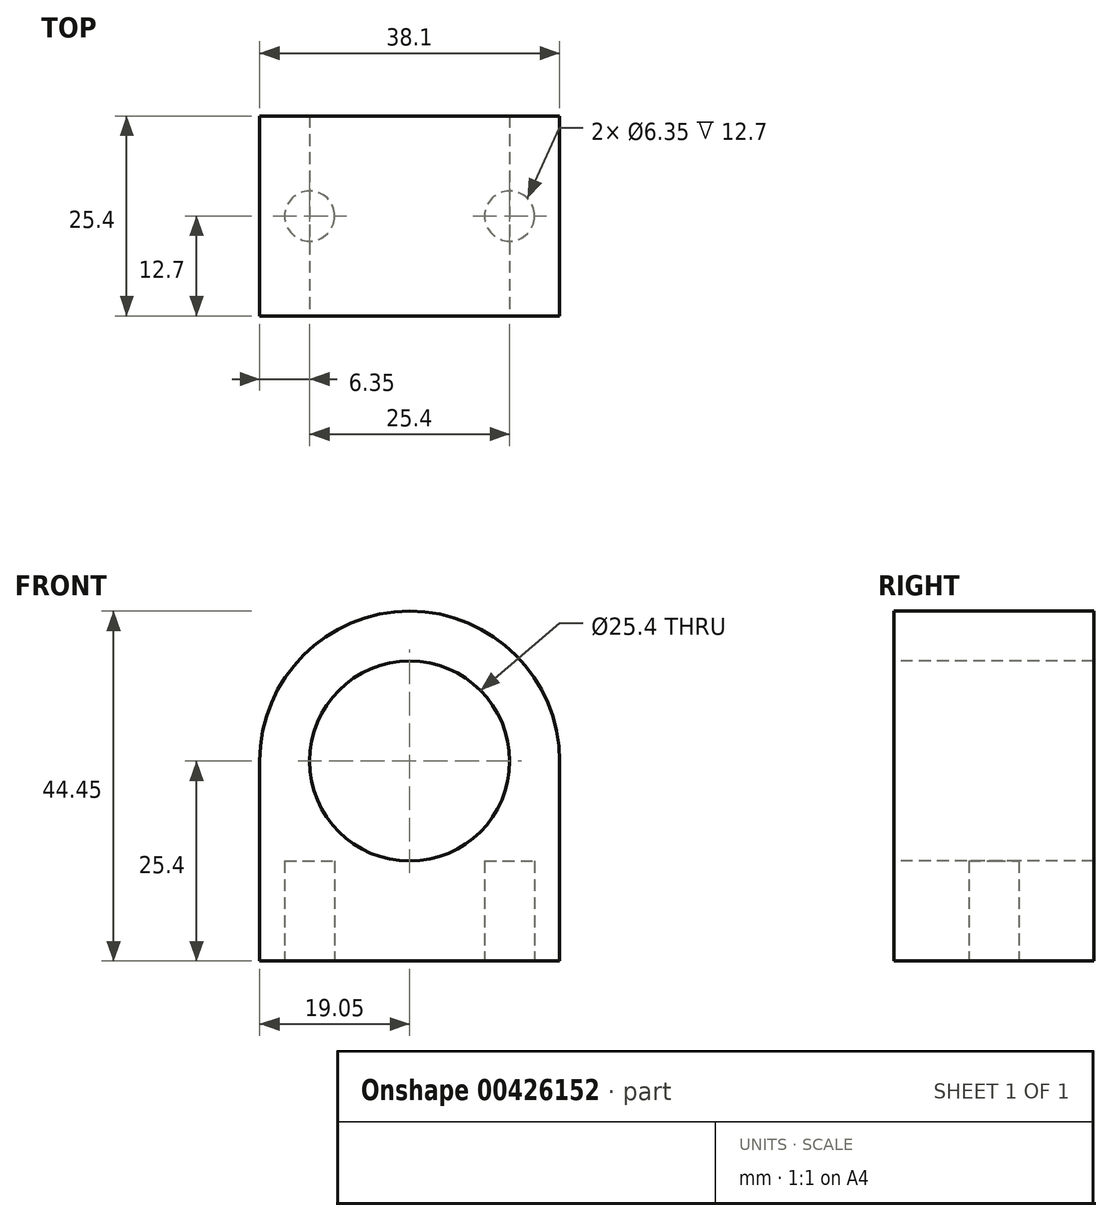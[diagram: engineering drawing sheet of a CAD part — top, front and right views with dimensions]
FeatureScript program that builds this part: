
annotation { "Feature Type Name" : "Feature", "Feature Type Description" : "" }
export const myFeature = defineFeature(function(context is Context, id is Id, definition is map)
    precondition{}
    {
        {
            var Q0;
            Q0=qCreatedBy(makeId("Front.planeOp"),FACE);
            var sketch = newSketch(context, id + "F0", { "sketchPlane" : qUnion([Q0])});
            skLineSegment(sketch, "E0.top", {"start": v(-19.05, -25.4) * mm, "end": v(19.05, -25.4) * mm});
            skLineSegment(sketch, "E0.left", {"start": v(-19.05, 0) * mm, "end": v(-19.05, -25.4) * mm});
            skLineSegment(sketch, "E0.right", {"start": v(19.05, 0) * mm, "end": v(19.05, -25.4) * mm});
            skArc(sketch, "E1", {"start": v(19.05, 0) * mm, "mid": v(0, 19.05) * mm, "end": v(-19.05, 0) * mm});
            skSolve(sketch);
        }
        {
            var Q0;
            Q0 = qSketchRegion(id + "F0", true);
            extrude(context, id + "F1", {"entities" : qUnion([Q0]), "endBound" : BoundingType.SYMMETRIC, "depth" : 25.4 * mm});
        }
        {
            var Q0;
            Q0=makeQuery(id+"F1.opExtrude","CAP_FACE",FACE,{"disambiguationData":[OSD([sQuery(id+"F0.wireOp",EDGE,"E0.top"),sQuery(id+"F0.wireOp",EDGE,"E0.left"),sQuery(id+"F0.wireOp",EDGE,"E0.right"),sQuery(id+"F0.wireOp",EDGE,"E1")])],"isStart":false});
            var sketch = newSketch(context, id + "F2", { "sketchPlane" : qUnion([Q0])});
            skCircle(sketch, "E2", {"center": v(0, 0) * mm, "radius": 12.7 * mm});
            skSolve(sketch);
        }
        {
            var Q0;
            Q0 = qSketchRegion(id + "F2", true);
            extrude(context, id + "F3", {"entities" : qUnion([Q0]), "operationType" : NewBodyOperationType.REMOVE, "endBound" : BoundingType.THROUGH_ALL, "oppositeDirection" : true, "depth" : 25.4 * mm});
        }
        {
            var Q0;
            Q0=makeQuery(id+"F1.opExtrude","SWEPT_FACE",FACE,{"disambiguationData":[OSD([sQuery(id+"F0.wireOp",EDGE,"E0.top")])]});
            var sketch = newSketch(context, id + "F4", { "sketchPlane" : qUnion([Q0])});
            skCircle(sketch, "E3", {"center": v(-12.7, 0) * mm, "radius": 3.18 * mm});
            skCircle(sketch, "E4", {"center": v(12.7, 0) * mm, "radius": 3.18 * mm});
            skSolve(sketch);
        }
        {
            var Q0;
            Q0 = qSketchRegion(id + "F4", true);
            extrude(context, id + "F5", {"entities" : qUnion([Q0]), "operationType" : NewBodyOperationType.REMOVE, "oppositeDirection" : true, "depth" : 12.7 * mm});
        }
    });
